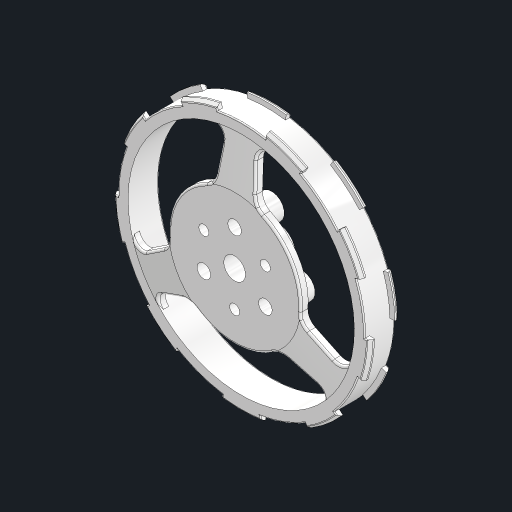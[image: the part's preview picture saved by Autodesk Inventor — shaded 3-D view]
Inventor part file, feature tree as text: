
AUTODESK INVENTOR PART (.ipt)
format: ipt  version: 2023.2 (Build 272271030, 271C)  size: 958,464 bytes
history: native  units: mm
features: sketch x19, extrude x14, fillet x7, pattern_circular x5, revolve x3, other x2, chamfer x2, projected_geometry x2
ambient origin geometry x8: Origin, YZ Plane, XZ Plane, XY Plane, X Axis, Y Axis, Z Axis, Center Point
bodies: Body1 (feature_tree)
feature tree (54):
  other  "ソリッド1"
  extrude  "押し出し1"  Depth=50.6mm
  extrude  "押し出し2"  Depth=7.3mm TaperAngle=0.0deg
  sketch  "スケッチ3"
  revolve  "回転1"
  extrude  "押し出し3"  Depth=3.0mm
  revolve  "回転2"
  chamfer  "面取り1"  Distance=1.3mm
  chamfer  "面取り2"  Distance=26.0mm
  extrude  "押し出し4"  TaperAngle=90.0deg  [1 undecoded]
  pattern_circular  "円形状パターン1"  [2 undecoded]
  extrude  "押し出し5"  Depth=3.0mm
  pattern_circular  "円形状パターン2"  [2 undecoded]
  extrude  "押し出し6"  Depth=4.0mm
  extrude  "押し出し7"  Depth=30.0mm TaperAngle=360.0deg
  revolve  "回転3"
  extrude  "押し出し8"  TaperAngle=0.0deg  [1 undecoded]
  pattern_circular  "円形状パターン3"  [2 undecoded]
  extrude  "押し出し9"  Depth=1.0mm
  extrude  "押し出し10"  Depth=1.0mm
  extrude  "押し出し11"  TaperAngle=90.0deg  [1 undecoded]
  pattern_circular  "円形状パターン4"  Angle=45.0deg  [1 undecoded]
  extrude  "押し出し12"  Depth=0.7mm TaperAngle=45.0deg
  extrude  "押し出し13"  Depth=5.0mm
  pattern_circular  "円形状パターン5"  [2 undecoded]
  sketch  "スケッチ18"
  other  "作業平面1"
  extrude  "押し出し14"  TaperAngle=180.0deg  [1 undecoded]
  fillet  "フィレット1"  Radius=1.3mm
  fillet  "フィレット2"  Radius=90.0mm
  fillet  "フィレット3"  Radius=5.0mm
  fillet  "フィレット4"  Radius=5.0mm
  fillet  "フィレット5"  Radius=1.3mm
  fillet  "フィレット6"  Radius=90.0mm
  fillet  "フィレット7"  Radius=4.5mm
  sketch  "スケッチ1"
  sketch  "スケッチ2"
  sketch  "スケッチ4"
  sketch  "スケッチ5"
  projected_geometry  "投影ループ1"
  projected_geometry  "投影ループ2"
  sketch  "スケッチ6"
  sketch  "スケッチ7"
  sketch  "スケッチ8"
  sketch  "スケッチ9"
  sketch  "スケッチ10"
  sketch  "スケッチ11"
  sketch  "スケッチ12"
  sketch  "スケッチ13"
  sketch  "スケッチ14"
  sketch  "スケッチ15"
  sketch  "スケッチ16"
  sketch  "スケッチ17"
  sketch  "スケッチ19"
note: 13 required parameter values undecoded (feature->parameter linkage not recoverable at this tier; creation-order binding heuristic only, values carry confidence <= 0.55)
